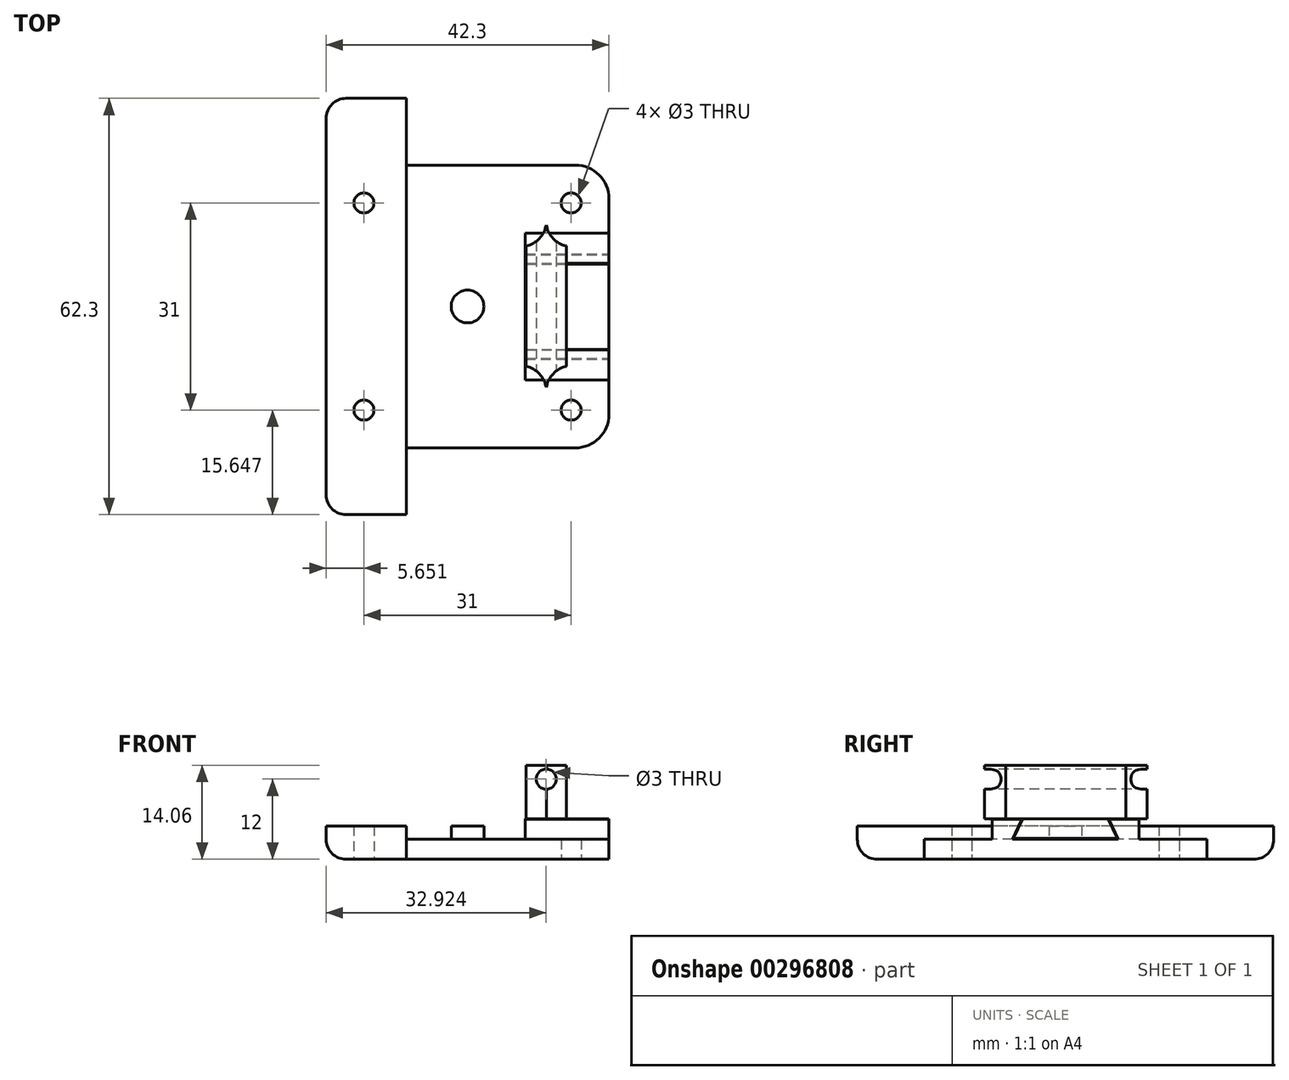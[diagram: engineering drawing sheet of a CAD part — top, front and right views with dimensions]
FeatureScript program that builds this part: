
annotation { "Feature Type Name" : "Feature", "Feature Type Description" : "" }
export const myFeature = defineFeature(function(context is Context, id is Id, definition is map)
    precondition{}
    {
        {
            assignVariable(context, id + "F0", {"name" : "NbaseWidth", "anyValue" : 42.3});
        }
        {
            var Q0;
            Q0=qCreatedBy(makeId("Top.planeOp"),FACE);
            var sketch = newSketch(context, id + "F1", { "sketchPlane" : qUnion([Q0])});
            skLineSegment(sketch, "E0.bottom", {"start": v(-19.96, 20.05) * mm, "end": v(17.34, 20.05) * mm});
            skLineSegment(sketch, "E0.top", {"start": v(-19.96, -22.25) * mm, "end": v(17.34, -22.25) * mm});
            skLineSegment(sketch, "E0.left", {"start": v(-19.96, 20.05) * mm, "end": v(-19.96, -22.25) * mm});
            skLineSegment(sketch, "E0.right", {"start": v(22.34, 15.05) * mm, "end": v(22.34, -17.25) * mm});
            skPoint(sketch, "E1", {"position": v(-14.3, 14.4) * mm});
            skPoint(sketch, "E2.0.1.0", {"position": v(-14.3, -16.6) * mm});
            skPoint(sketch, "E2.1.0.0", {"position": v(16.7, 14.4) * mm});
            skPoint(sketch, "E2.1.1.0", {"position": v(16.7, -16.6) * mm});
            skLineSegment(sketch, "E2.direction1", {"start": v(-14.3, 14.4) * mm, "end": v(16.7, 14.4) * mm, "construction": true});
            skLineSegment(sketch, "E2.direction2", {"start": v(-14.3, 14.4) * mm, "end": v(-14.3, -16.6) * mm, "construction": true});
            skCircle(sketch, "E3", {"center": v(-14.3, 14.4) * mm, "radius": 1.5 * mm});
            skCircle(sketch, "E4", {"center": v(16.7, 14.4) * mm, "radius": 1.5 * mm});
            skCircle(sketch, "E5", {"center": v(16.7, -16.6) * mm, "radius": 1.5 * mm});
            skCircle(sketch, "E6", {"center": v(-14.3, -16.6) * mm, "radius": 1.5 * mm});
            skCircle(sketch, "E7", {"center": v(1.2, -1.1) * mm, "radius": 2.45 * mm});
            skCircle(sketch, "E8", {"center": v(1.2, -1.1) * mm, "radius": 3.5 * mm, "construction": true});
            skPoint(sketch, "E9.visualSharp", {"position": v(22.34, 20.05) * mm});
            skArc(sketch, "E9.filletArc", {"start": v(22.34, 15.05) * mm, "mid": v(20.88, 18.58) * mm, "end": v(17.34, 20.05) * mm});
            skPoint(sketch, "E10.visualSharp", {"position": v(22.34, -22.25) * mm});
            skArc(sketch, "E10.filletArc", {"start": v(17.34, -22.25) * mm, "mid": v(20.88, -20.79) * mm, "end": v(22.34, -17.25) * mm});
            skLineSegment(sketch, "E11.bottom", {"start": v(-19.96, -22.25) * mm, "end": v(-7.96, -22.25) * mm});
            skLineSegment(sketch, "E11.top", {"start": v(-19.96, -32.25) * mm, "end": v(-7.96, -32.25) * mm});
            skLineSegment(sketch, "E11.left", {"start": v(-19.96, -22.25) * mm, "end": v(-19.96, -32.25) * mm});
            skLineSegment(sketch, "E11.right", {"start": v(-7.96, -22.25) * mm, "end": v(-7.96, -32.25) * mm});
            skLineSegment(sketch, "E12.bottom", {"start": v(-19.96, 20.05) * mm, "end": v(-7.96, 20.05) * mm});
            skLineSegment(sketch, "E12.top", {"start": v(-19.96, 30.05) * mm, "end": v(-7.96, 30.05) * mm});
            skLineSegment(sketch, "E12.left", {"start": v(-19.96, 20.05) * mm, "end": v(-19.96, 30.05) * mm});
            skLineSegment(sketch, "E12.right", {"start": v(-7.96, 20.05) * mm, "end": v(-7.96, 30.05) * mm});
            skSolve(sketch);
        }
        {
            var Q0;
            {var subQ0=sQuery(id+"F1.wireOp",EDGE,"E0.left");Q0=makeQuery(id+"F1.imprint","IMPRINT",FACE,{"disambiguationData":[TD([[makeQuery(id+"F1.imprint","IMPRINT",EDGE,{"derivedFrom":subQ0}),1.0]])]});}
            extrude(context, id + "F2", {"entities" : qUnion([Q0]), "depth" : 3 * mm});
        }
        {
            var Q0;
            Q0=makeQuery(id+"F2.opExtrude","CAP_FACE",FACE,{"disambiguationData":[OSD([sQuery(id+"F1.wireOp",EDGE,"E0.bottom"),sQuery(id+"F1.wireOp",EDGE,"E0.top"),sQuery(id+"F1.wireOp",EDGE,"E0.left"),sQuery(id+"F1.wireOp",EDGE,"E0.right"),sQuery(id+"F1.wireOp",EDGE,"E3"),sQuery(id+"F1.wireOp",EDGE,"E4"),sQuery(id+"F1.wireOp",EDGE,"E5"),sQuery(id+"F1.wireOp",EDGE,"E6"),sQuery(id+"F1.wireOp",EDGE,"E7"),sQuery(id+"F1.wireOp",EDGE,"E9.filletArc"),sQuery(id+"F1.wireOp",EDGE,"E10.filletArc")])],"isStart":false});
            var sketch = newSketch(context, id + "F3", { "sketchPlane" : qUnion([Q0])});
            skCircle(sketch, "E13", {"center": v(16.7, 14.4) * mm, "radius": 2.23 * mm});
            skCircle(sketch, "E14", {"center": v(16.7, -16.6) * mm, "radius": 2.45 * mm});
            skCircle(sketch, "E15", {"center": v(1.2, -1.1) * mm, "radius": 4.3 * mm});
            skCircle(sketch, "E16", {"center": v(-14.3, 14.4) * mm, "radius": 3.3 * mm});
            skCircle(sketch, "E17", {"center": v(-14.3, -16.6) * mm, "radius": 3.3 * mm});
            skLineSegment(sketch, "E18.bottom", {"start": v(-19.96, 20.05) * mm, "end": v(-7.96, 20.05) * mm});
            skLineSegment(sketch, "E18.top", {"start": v(-19.96, -22.25) * mm, "end": v(-7.96, -22.25) * mm});
            skLineSegment(sketch, "E18.left", {"start": v(-19.96, 20.05) * mm, "end": v(-19.96, -22.25) * mm});
            skLineSegment(sketch, "E18.right", {"start": v(-7.96, 20.05) * mm, "end": v(-7.96, -22.25) * mm});
            skSolve(sketch);
        }
        {
            var Q0;
            Q0=makeQuery(id+"F3.imprint","IMPRINT",FACE,{"disambiguationData":[TD([[makeQuery(id+"F3.imprint","IMPRINT",EDGE,{"derivedFrom":sQuery(id+"F3.wireOp",EDGE,"E16")}),-1.0]])]});
            var Q1;
            Q1=makeQuery(id+"F3.imprint","IMPRINT",FACE,{"disambiguationData":[TD([[makeQuery(id+"F3.imprint","IMPRINT",EDGE,{"derivedFrom":sQuery(id+"F3.wireOp",EDGE,"E16")}),1.0]])]});
            var Q2;
            Q2=makeQuery(id+"F3.imprint","IMPRINT",FACE,{"disambiguationData":[TD([[makeQuery(id+"F3.imprint","IMPRINT",EDGE,{"derivedFrom":sQuery(id+"F3.wireOp",EDGE,"E17")}),1.0]])]});
            extrude(context, id + "F4", {"entities" : qUnion([Q0, Q1, Q2]), "operationType" : NewBodyOperationType.ADD, "depth" : 2 * mm});
        }
        {
            var Q0;
            Q0=makeQuery(id+"F1.imprint","IMPRINT",FACE,{"disambiguationData":[TD([[makeQuery(id+"F1.imprint","IMPRINT",EDGE,{"derivedFrom":sQuery(id+"F1.wireOp",EDGE,"E12.top")}),-1.0]])]});
            var Q1;
            Q1=makeQuery(id+"F1.imprint","IMPRINT",FACE,{"disambiguationData":[TD([[makeQuery(id+"F1.imprint","IMPRINT",EDGE,{"derivedFrom":sQuery(id+"F1.wireOp",EDGE,"E11.top")}),1.0]])]});
            var Q2;
            Q2=makeQuery(id+"F3.imprint","IMPRINT",FACE,{"disambiguationData":[TD([[makeQuery(id+"F3.imprint","IMPRINT",EDGE,{"derivedFrom":sQuery(id+"F3.wireOp",EDGE,"be03cbd9-48ab-4eb9-bd98-74e1857a0f09.0")}),-1.0]])]});
            extrude(context, id + "F5", {"entities" : qUnion([Q0, Q1, Q2]), "operationType" : NewBodyOperationType.ADD, "depth" : 2 * mm});
        }
        {
            var Q0;
            Q0=makeQuery(id+"F5.opExtrude","SWEPT_EDGE",EDGE,{"disambiguationData":[OSD([sQuery(id+"F1.wireOp",EDGE,"E11.top"),sQuery(id+"F1.wireOp",EDGE,"E11.left")])]});
            var Q1;
            Q1=makeQuery(id+"F5.opExtrude","SWEPT_EDGE",EDGE,{"disambiguationData":[OSD([sQuery(id+"F1.wireOp",EDGE,"E12.top"),sQuery(id+"F1.wireOp",EDGE,"E12.left")])]});
            fillet(context, id + "F6", {"entities" : qUnion([Q0, Q1]), "radius" : 3 * mm, "tangentPropagation" : true, "allowEdgeOverflow" : false});
        }
        {
            var Q0;
            Q0=makeQuery(id+"F3.imprint","IMPRINT",FACE,{"disambiguationData":[TD([[makeQuery(id+"F3.imprint","IMPRINT",EDGE,{"derivedFrom":makeQuery(id+"F2.opExtrude","CAP_EDGE",EDGE,{"disambiguationData":[OSD([sQuery(id+"F1.wireOp",EDGE,"E7")])],"isStart":false})}),1.0]])]});
            extrude(context, id + "F7", {"entities" : qUnion([Q0]), "operationType" : NewBodyOperationType.ADD, "depth" : 2 * mm, "hasSecondDirection" : true, "secondDirectionOppositeDirection" : true, "secondDirectionDepth" : 3 * mm});
        }
        {
            var Q0;
            Q0=makeQuery(id+"F5.opExtrude","CAP_FACE",FACE,{"disambiguationData":[OSD([sQuery(id+"F1.wireOp",EDGE,"E0.bottom"),sQuery(id+"F1.wireOp",EDGE,"E12.top"),sQuery(id+"F1.wireOp",EDGE,"E12.left"),sQuery(id+"F1.wireOp",EDGE,"E12.right")])],"isStart":false});
            var Q1;
            Q1=makeQuery(id+"F5.opExtrude","CAP_FACE",FACE,{"disambiguationData":[OSD([sQuery(id+"F1.wireOp",EDGE,"E0.top"),sQuery(id+"F1.wireOp",EDGE,"E11.top"),sQuery(id+"F1.wireOp",EDGE,"E11.left"),sQuery(id+"F1.wireOp",EDGE,"E11.right")])],"isStart":false});
            extrude(context, id + "F8", {"entities" : qUnion([Q0, Q1]), "operationType" : NewBodyOperationType.ADD, "depth" : 3 * mm});
        }
        {
            var Q0;
            Q0=makeQuery(id+"F5.boolean.opBoolean","MERGE",EDGE,{"derivedFrom":[makeQuery(id+"F2.opExtrude","CAP_EDGE",EDGE,{"disambiguationData":[OSD([sQuery(id+"F1.wireOp",EDGE,"E0.left")])],"isStart":true}),makeQuery(id+"F5.opExtrude","CAP_EDGE",EDGE,{"disambiguationData":[OSD([sQuery(id+"F1.wireOp",EDGE,"E11.left")])],"isStart":true}),makeQuery(id+"F5.opExtrude","CAP_EDGE",EDGE,{"disambiguationData":[OSD([sQuery(id+"F1.wireOp",EDGE,"E12.left")])],"isStart":true})]});
            fillet(context, id + "F9", {"entities" : qUnion([Q0]), "radius" : 3 * mm, "tangentPropagation" : true, "allowEdgeOverflow" : false});
        }
        {
            var Q0;
            Q0=makeQuery(id+"F3.imprint","IMPRINT",FACE,{"disambiguationData":[TD([[makeQuery(id+"F3.imprint","IMPRINT",EDGE,{"derivedFrom":sQuery(id+"F3.wireOp",EDGE,"E13")}),-1.0]])]});
            var sketch = newSketch(context, id + "F10", { "sketchPlane" : qUnion([Q0])});
            skLineSegment(sketch, "E19.bottom", {"start": v(22.34, 9.9) * mm, "end": v(9.84, 9.9) * mm});
            skLineSegment(sketch, "E19.top", {"start": v(22.34, -12.1) * mm, "end": v(9.84, -12.1) * mm});
            skLineSegment(sketch, "E19.left", {"start": v(22.34, 9.9) * mm, "end": v(22.34, -12.1) * mm});
            skLineSegment(sketch, "E19.right", {"start": v(9.84, 9.9) * mm, "end": v(9.84, -12.1) * mm});
            skLineSegment(sketch, "E20", {"start": v(12.97, -12.1) * mm, "end": v(12.97, 9.9) * mm, "construction": true});
            skSolve(sketch);
        }
        {
            var Q0;
            Q0=makeQuery(id+"F10.imprint","IMPRINT",FACE,{"disambiguationData":[TD([[makeQuery(id+"F10.imprint","IMPRINT",EDGE,{"derivedFrom":sQuery(id+"F10.wireOp",EDGE,"E19.bottom")}),1.0]])]});
            extrude(context, id + "F11", {"entities" : qUnion([Q0]), "operationType" : NewBodyOperationType.ADD, "depth" : 3 * mm});
        }
        {
            var Q0;
            Q0=makeQuery(id+"F11.boolean.opBoolean","MERGE",FACE,{"derivedFrom":[makeQuery(id+"F2.opExtrude","SWEPT_FACE",FACE,{"disambiguationData":[OSD([sQuery(id+"F1.wireOp",EDGE,"E0.right")])]}),makeQuery(id+"F11.opExtrude","SWEPT_FACE",FACE,{"disambiguationData":[OSD([sQuery(id+"F10.wireOp",EDGE,"E19.left")])]})]});
            var sketch = newSketch(context, id + "F12", { "sketchPlane" : qUnion([Q0])});
            skLineSegment(sketch, "E21", {"start": v(-7.6, 6) * mm, "end": v(-9, 3) * mm});
            skLineSegment(sketch, "E22", {"start": v(-1.1, 6) * mm, "end": v(-1.1, 3) * mm, "construction": true});
            skLineSegment(sketch, "E23.MirrorCS", {"start": v(5.4, 6) * mm, "end": v(6.8, 3) * mm});
            skLineSegment(sketch, "E24", {"start": v(-9, 3) * mm, "end": v(6.8, 3) * mm});
            skSolve(sketch);
        }
        {
            var Q0;
            {var subQ0=sQuery(id+"F12.wireOp",EDGE,"E21");Q0=makeQuery(id+"F12.imprint","IMPRINT",FACE,{"disambiguationData":[TD([[makeQuery(id+"F12.imprint","IMPRINT",EDGE,{"derivedFrom":subQ0}),1.0]])]});}
            extrude(context, id + "F13", {"entities" : qUnion([Q0]), "operationType" : NewBodyOperationType.REMOVE, "oppositeDirection" : true, "depth" : 13 * mm});
        }
        {
            var Q0;
            {var subQ11=sQuery(id+"F12.wireOp",EDGE,"E21");Q0=makeQuery(id+"F12.imprint","IMPRINT",FACE,{"disambiguationData":[TD([[makeQuery(id+"F12.imprint","IMPRINT",EDGE,{"derivedFrom":subQ11}),-1.0]])]});}
            var sketch = newSketch(context, id + "F14", { "sketchPlane" : qUnion([Q0])});
            skLineSegment(sketch, "E25", {"start": v(-1.1, 6) * mm, "end": v(-1.1, 3) * mm, "construction": true});
            skLineSegment(sketch, "E26.0", {"start": v(5.25, 6.06) * mm, "end": v(6.62, 3.11) * mm});
            skLineSegment(sketch, "E26.1", {"start": v(-8.89, 3.11) * mm, "end": v(6.62, 3.11) * mm});
            skLineSegment(sketch, "E26.2", {"start": v(-7.51, 6.06) * mm, "end": v(-8.89, 3.11) * mm});
            skLineSegment(sketch, "E27", {"start": v(5.25, 6.06) * mm, "end": v(-7.51, 6.06) * mm});
            skSolve(sketch);
        }
        {
            var Q0;
            Q0=qSketchRegion(id+"F14",true);
            extrude(context, id + "F15", {"entities" : qUnion([Q0]), "operationType" : NewBodyOperationType.ADD, "oppositeDirection" : true, "depth" : 12.5 * mm});
        }
        {
            var Q0;
            Q0=makeQuery(id+"F15.opExtrude","SWEPT_FACE",FACE,{"disambiguationData":[OSD([sQuery(id+"F14.wireOp",EDGE,"E27")])]});
            var sketch = newSketch(context, id + "F16", { "sketchPlane" : qUnion([Q0])});
            skLineSegment(sketch, "E28", {"start": v(12.97, -22.16) * mm, "end": v(12.97, 19.84) * mm, "construction": true});
            skLineSegment(sketch, "E29.right", {"start": v(9.97, 7.95) * mm, "end": v(9.97, -10.04) * mm});
            skLineSegment(sketch, "E30", {"start": v(12.97, 17.1) * mm, "end": v(12.97, -18.24) * mm, "construction": true});
            skArc(sketch, "E31", {"start": v(9.97, 7.95) * mm, "mid": v(11.93, 9.08) * mm, "end": v(12.97, 11.1) * mm});
            skArc(sketch, "E32", {"start": v(12.97, -13.2) * mm, "mid": v(11.93, -11.18) * mm, "end": v(9.97, -10.04) * mm});
            skArc(sketch, "E33.MirrorCS", {"start": v(15.97, 7.95) * mm, "mid": v(14, 9.08) * mm, "end": v(12.97, 11.1) * mm});
            skLineSegment(sketch, "E34.MirrorCS", {"start": v(15.97, 7.95) * mm, "end": v(15.97, -10.04) * mm});
            skArc(sketch, "E35.MirrorCS", {"start": v(12.97, -13.2) * mm, "mid": v(14, -11.18) * mm, "end": v(15.97, -10.04) * mm});
            skSolve(sketch);
        }
        {
            var Q0;
            {var subQ4=sQuery(id+"F16.wireOp",EDGE,"E31");Q0=makeQuery(id+"F16.imprint","IMPRINT",FACE,{"disambiguationData":[TD([[makeQuery(id+"F16.imprint","IMPRINT",EDGE,{"derivedFrom":subQ4}),-1.0]])]});}
            var Q1;
            {var subQ0=sQuery(id+"F16.wireOp",EDGE,"E29.right");var subQ1=sQuery(id+"F14.wireOp",EDGE,"2Cx5xiBh-8RA7-QqPe-MKKm-lHO9sfmHYvEv");var subQ2=makeQuery(id+"F15.opExtrude","SWEPT_EDGE",EDGE,{"disambiguationData":[OSD([sQuery(id+"F14.wireOp",EDGE,"fP7R35G4-nflu-wZ0Q-w6Wp-tCEXwCJ3FfRi"),subQ1])]});var subQ3=makeQuery(id+"F16.imprint","INTERSECT",VERTEX,{"derivedFrom":[subQ2,subQ0]});Q1=makeQuery(id+"F16.imprint","IMPRINT",FACE,{"disambiguationData":[TD([[makeQuery(id+"F16.imprint","IMPRINT",EDGE,{"disambiguationData":[TD([[subQ3,-1.0]])],"derivedFrom":subQ0}),1.0]])]});}
            var Q2;
            {var subQ4=sQuery(id+"F16.wireOp",EDGE,"E32");Q2=makeQuery(id+"F16.imprint","IMPRINT",FACE,{"disambiguationData":[TD([[makeQuery(id+"F16.imprint","IMPRINT",EDGE,{"derivedFrom":subQ4}),-1.0]])]});}
            extrude(context, id + "F17", {"entities" : qUnion([Q0, Q1, Q2]), "operationType" : NewBodyOperationType.ADD, "depth" : 8 * mm});
        }
        {
            var Q0;
            Q0=makeQuery(id+"F4.boolean.opBoolean","MERGE",FACE,{"derivedFrom":[makeQuery(id+"F2.opExtrude","SWEPT_FACE",FACE,{"disambiguationData":[OSD([sQuery(id+"F1.wireOp",EDGE,"E0.top")])]}),makeQuery(id+"F4.opExtrude","SWEPT_FACE",FACE,{"disambiguationData":[OSD([sQuery(id+"F3.wireOp",EDGE,"E18.top")])]})]});
            var sketch = newSketch(context, id + "F18", { "sketchPlane" : qUnion([Q0])});
            skCircle(sketch, "E36", {"center": v(12.96, 12) * mm, "radius": 1.25 * mm});
            skSolve(sketch);
        }
        {
            var Q0;
            Q0=sQuery(id+"F18.wireOp",VERTEX,"E36.center");
            var Q1;
            Q1=makeQuery(id+"F15.opExtrude","SWEPT_BODY",BODY,{"disambiguationData":[OSD([sQuery(id+"F14.wireOp",EDGE,"E26.0"),sQuery(id+"F14.wireOp",EDGE,"E26.1"),sQuery(id+"F14.wireOp",EDGE,"E26.2"),sQuery(id+"F14.wireOp",EDGE,"fP7R35G4-nflu-wZ0Q-w6Wp-tCEXwCJ3FfRi"),sQuery(id+"F14.wireOp",EDGE,"2Cx5xiBh-8RA7-QqPe-MKKm-lHO9sfmHYvEv"),sQuery(id+"F14.wireOp",EDGE,"dFcceF2f-2LQF-KBSS-Kckc-Tti9Hr8d2nyk")])]});
            hole(context, id + "F19", {"style" : HoleStyle.SIMPLE, "endStyle" : HoleEndStyle.BLIND, "holeDiameter" : 3 * mm, "holeDepth" : (getVariable(context, 'NbaseWidth')) * mm, "tappedDepth" : 12 * mm, "tapClearance" : 3, "locations" : qUnion([Q0]), "scope" : qUnion([Q1])});
        }
    });
